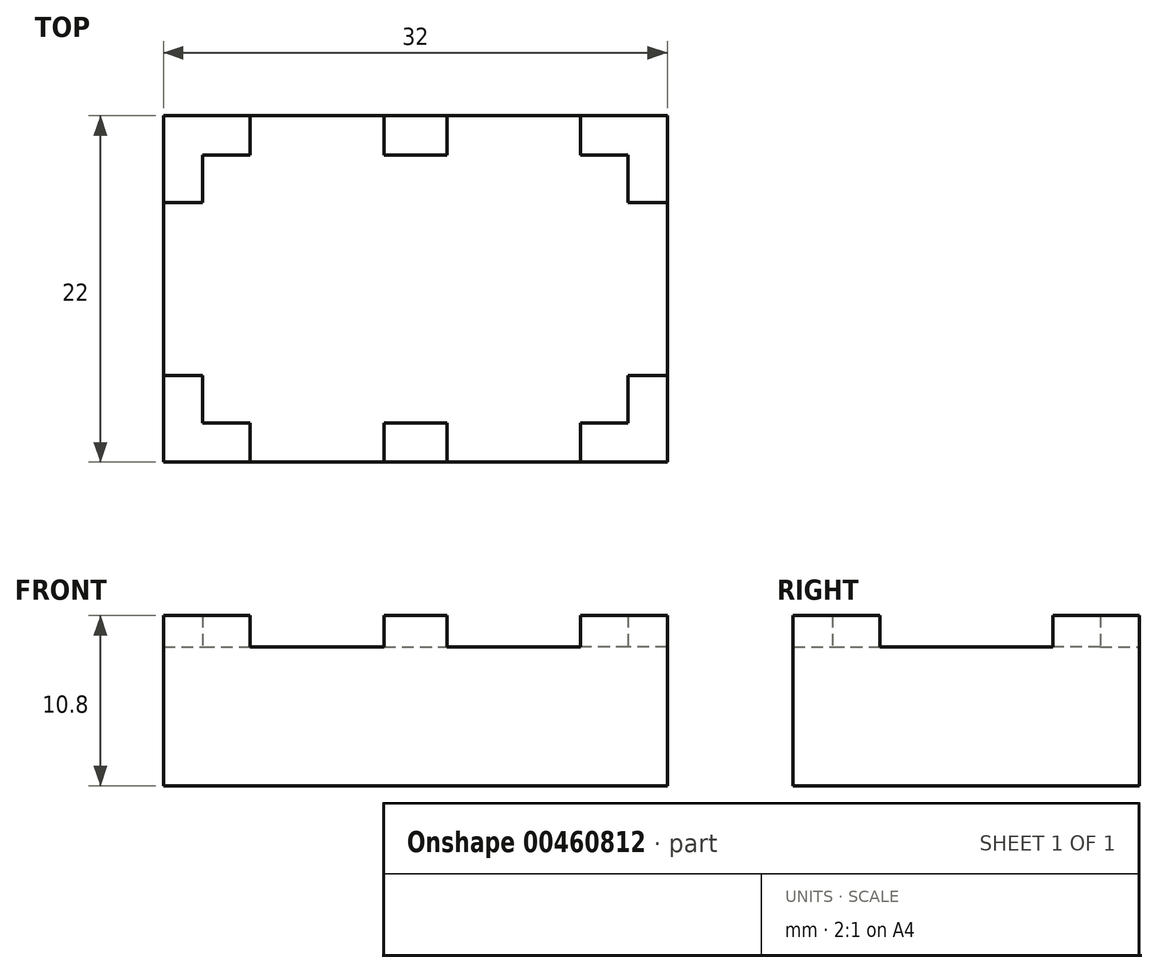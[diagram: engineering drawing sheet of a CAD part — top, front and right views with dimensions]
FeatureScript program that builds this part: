
annotation { "Feature Type Name" : "Feature", "Feature Type Description" : "" }
export const myFeature = defineFeature(function(context is Context, id is Id, definition is map)
    precondition{}
    {
        {
            var Q0;
            Q0=qCreatedBy(makeId("Top.planeOp"),FACE);
            var sketch = newSketch(context, id + "F0", { "sketchPlane" : qUnion([Q0])});
            skLineSegment(sketch, "E0.bottom", {"start": v(0, 0) * mm, "end": v(-16, 0) * mm});
            skLineSegment(sketch, "E0.top", {"start": v(0, 11) * mm, "end": v(-16, 11) * mm});
            skLineSegment(sketch, "E0.left", {"start": v(0, 0) * mm, "end": v(0, 11) * mm});
            skLineSegment(sketch, "E0.right", {"start": v(-16, 0) * mm, "end": v(-16, 11) * mm});
            skSolve(sketch);
        }
        {
            var Q0;
            Q0 = qSketchRegion(id + "F0", true);
            extrude(context, id + "F1", {"entities" : qUnion([Q0]), "depth" : 5 * mm});
        }
        {
            var Q0;
            Q0=makeQuery(id+"F1.opExtrude","CAP_FACE",FACE,{"disambiguationData":[OSD([sQuery(id+"F0.wireOp",EDGE,"E0.bottom"),sQuery(id+"F0.wireOp",EDGE,"E0.top"),sQuery(id+"F0.wireOp",EDGE,"E0.left"),sQuery(id+"F0.wireOp",EDGE,"E0.right")])],"isStart":false});
            var sketch = newSketch(context, id + "F2", { "sketchPlane" : qUnion([Q0])});
            skLineSegment(sketch, "E1.bottom", {"start": v(-16, 11) * mm, "end": v(-10.5, 11) * mm});
            skLineSegment(sketch, "E1.top", {"start": v(-16, 8.5) * mm, "end": v(-10.5, 8.5) * mm});
            skLineSegment(sketch, "E1.left", {"start": v(-16, 11) * mm, "end": v(-16, 8.5) * mm});
            skLineSegment(sketch, "E1.right", {"start": v(-10.5, 11) * mm, "end": v(-10.5, 8.5) * mm});
            skLineSegment(sketch, "E2.bottom", {"start": v(-16, 11) * mm, "end": v(-13.5, 11) * mm});
            skLineSegment(sketch, "E2.top", {"start": v(-16, 5.5) * mm, "end": v(-13.5, 5.5) * mm});
            skLineSegment(sketch, "E2.left", {"start": v(-16, 11) * mm, "end": v(-16, 5.5) * mm});
            skLineSegment(sketch, "E2.right", {"start": v(-13.5, 11) * mm, "end": v(-13.5, 5.5) * mm});
            skLineSegment(sketch, "E3.bottom", {"start": v(-2, 8.5) * mm, "end": v(0, 8.5) * mm});
            skLineSegment(sketch, "E3.top", {"start": v(-2, 11) * mm, "end": v(0, 11) * mm});
            skLineSegment(sketch, "E3.left", {"start": v(-2, 8.5) * mm, "end": v(-2, 11) * mm});
            skLineSegment(sketch, "E3.right", {"start": v(0, 8.5) * mm, "end": v(0, 11) * mm});
            skSolve(sketch);
        }
        {
            var Q0;
            {var subQ5=sQuery(id+"F2.wireOp",EDGE,"E2.bottom");Q0=makeQuery(id+"F2.imprint","IMPRINT",FACE,{"disambiguationData":[TD([[makeQuery(id+"F2.imprint","IMPRINT",EDGE,{"derivedFrom":subQ5}),1.0]])]});}
            var Q1;
            {var subQ0=sQuery(id+"F2.wireOp",EDGE,"E1.bottom");Q1=makeQuery(id+"F2.imprint","IMPRINT",FACE,{"disambiguationData":[TD([[makeQuery(id+"F2.imprint","IMPRINT",EDGE,{"derivedFrom":subQ0}),1.0]])]});}
            var Q2;
            {var subQ5=sQuery(id+"F2.wireOp",EDGE,"E2.top");Q2=makeQuery(id+"F2.imprint","IMPRINT",FACE,{"disambiguationData":[TD([[makeQuery(id+"F2.imprint","IMPRINT",EDGE,{"derivedFrom":subQ5}),1.0]])]});}
            var Q3;
            Q3=makeQuery(id+"F2.imprint","IMPRINT",FACE,{"disambiguationData":[TD([[makeQuery(id+"F2.imprint","IMPRINT",EDGE,{"derivedFrom":sQuery(id+"F2.wireOp",EDGE,"E3.bottom")}),1.0]])]});
            extrude(context, id + "F3", {"entities" : qUnion([Q0, Q1, Q2, Q3]), "operationType" : NewBodyOperationType.ADD, "depth" : 2 * mm});
        }
        {
            var Q0;
            Q0=makeQuery(id+"F1.opExtrude","SWEPT_BODY",BODY,{"disambiguationData":[OSD([sQuery(id+"F0.wireOp",EDGE,"E0.bottom"),sQuery(id+"F0.wireOp",EDGE,"E0.top"),sQuery(id+"F0.wireOp",EDGE,"E0.left"),sQuery(id+"F0.wireOp",EDGE,"E0.right")])]});
            var Q1;
            Q1=qCreatedBy(makeId("Front.planeOp"),FACE);
            mirror(context, id + "F4", {"operationType" : NewBodyOperationType.ADD, "entities" : qUnion([Q0]), "mirrorPlane" : qUnion([Q1])});
        }
        {
            var Q0;
            Q0=makeQuery(id+"F1.opExtrude","SWEPT_BODY",BODY,{"disambiguationData":[OSD([sQuery(id+"F0.wireOp",EDGE,"E0.bottom"),sQuery(id+"F0.wireOp",EDGE,"E0.top"),sQuery(id+"F0.wireOp",EDGE,"E0.left"),sQuery(id+"F0.wireOp",EDGE,"E0.right")])]});
            var Q1;
            Q1=qCreatedBy(makeId("Right.planeOp"),FACE);
            mirror(context, id + "F5", {"operationType" : NewBodyOperationType.ADD, "entities" : qUnion([Q0]), "mirrorPlane" : qUnion([Q1])});
        }
        {
            var Q0;
            {var subQ0=makeQuery(id+"F1.opExtrude","CAP_FACE",FACE,{"disambiguationData":[OSD([sQuery(id+"F0.wireOp",EDGE,"E0.bottom"),sQuery(id+"F0.wireOp",EDGE,"E0.top"),sQuery(id+"F0.wireOp",EDGE,"E0.left"),sQuery(id+"F0.wireOp",EDGE,"E0.right")])],"isStart":true});var subQ1=makeQuery(id+"F4.boolean.opBoolean","MERGE",FACE,{"derivedFrom":[subQ0,makeQuery(id+"F4.opPattern","COPY",FACE,{"derivedFrom":subQ0,"instanceName":"1"})]});Q0=makeQuery(id+"F5.boolean.opBoolean","MERGE",FACE,{"derivedFrom":[subQ1,makeQuery(id+"F5.opPattern","COPY",FACE,{"derivedFrom":subQ1,"instanceName":"1"})]});}
            extrude(context, id + "F6", {"entities" : qUnion([Q0]), "operationType" : NewBodyOperationType.ADD, "depth" : 3.8 * mm});
        }
    });
